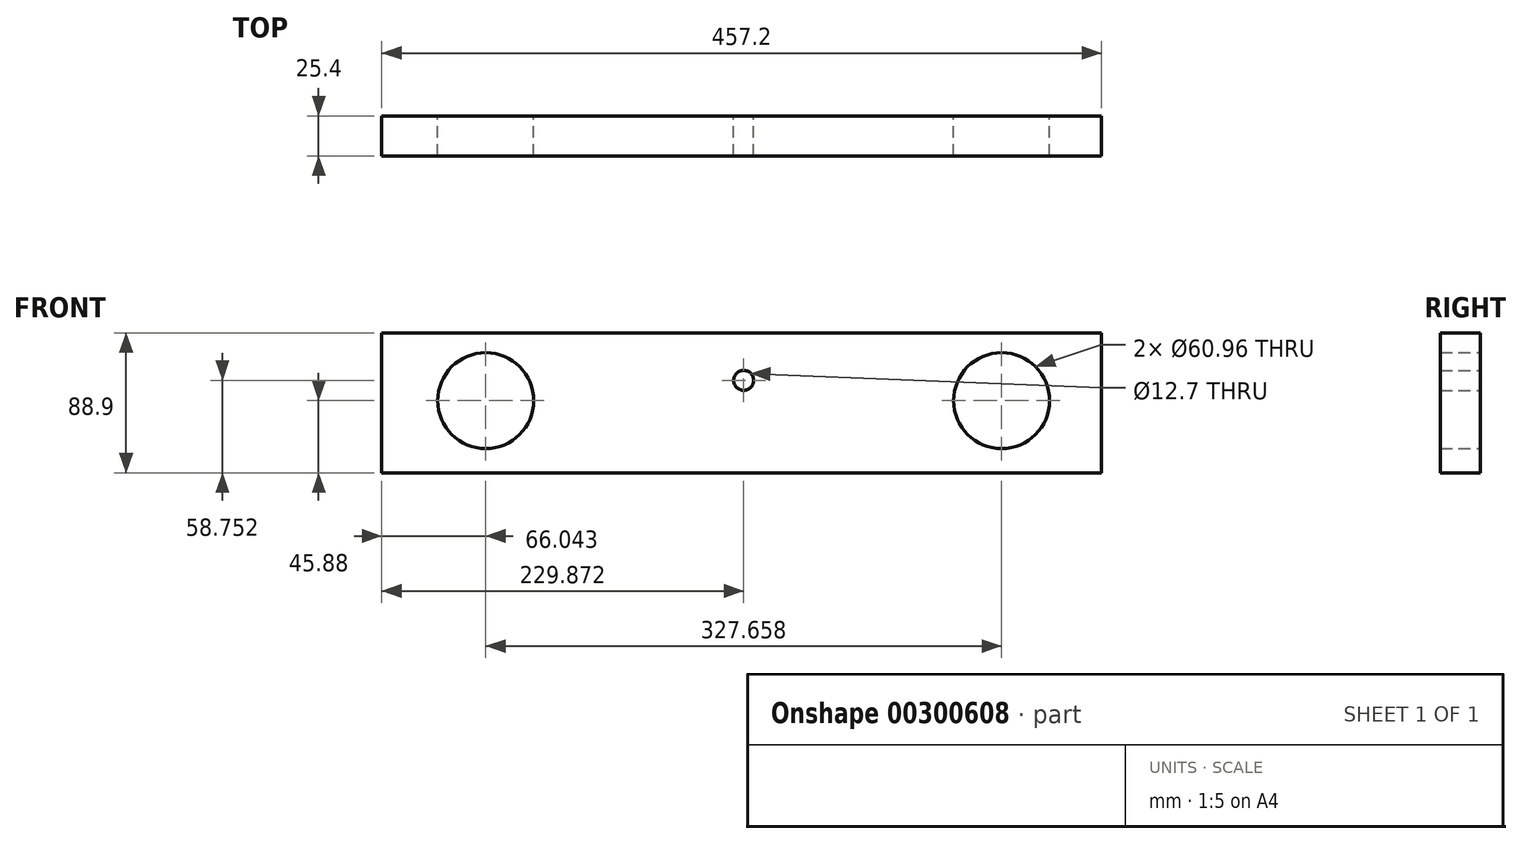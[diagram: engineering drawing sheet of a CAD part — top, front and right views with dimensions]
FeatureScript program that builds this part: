
annotation { "Feature Type Name" : "Feature", "Feature Type Description" : "" }
export const myFeature = defineFeature(function(context is Context, id is Id, definition is map)
    precondition{}
    {
        {
            var Q0;
            Q0=qCreatedBy(makeId("Front.planeOp"),FACE);
            var sketch = newSketch(context, id + "F0", { "sketchPlane" : qUnion([Q0])});
            skLineSegment(sketch, "E0", {"start": v(-310.3, 43.02) * mm, "end": v(-310.3, -45.88) * mm});
            skCircle(sketch, "E1", {"center": v(-244.27, 0) * mm, "radius": 30.48 * mm});
            skCircle(sketch, "E2", {"center": v(83.4, 0) * mm, "radius": 30.48 * mm});
            skPoint(sketch, "E3.endSnap0", {"position": v(273.9, -1.43) * mm});
            skLineSegment(sketch, "E4", {"start": v(-310.3, 43.02) * mm, "end": v(146.9, 43.02) * mm});
            skLineSegment(sketch, "E5", {"start": v(146.9, 43.02) * mm, "end": v(146.9, -45.88) * mm});
            skLineSegment(sketch, "E6", {"start": v(146.9, -45.88) * mm, "end": v(-310.3, -45.88) * mm});
            skLineSegment(sketch, "E7", {"start": v(-244.27, -30.48) * mm, "end": v(83.4, -30.48) * mm, "construction": true});
            skLineSegment(sketch, "E8", {"start": v(83.4, -30.48) * mm, "end": v(83.4, 30.48) * mm, "construction": true});
            skLineSegment(sketch, "E9", {"start": v(83.4, 30.48) * mm, "end": v(-244.27, 30.48) * mm, "construction": true});
            skLineSegment(sketch, "E10", {"start": v(-244.27, 30.48) * mm, "end": v(-244.27, -30.48) * mm, "construction": true});
            skCircle(sketch, "E11", {"center": v(-80.44, 12.87) * mm, "radius": 6.35 * mm});
            skPoint(sketch, "E11.centerSnap0", {"position": v(-80.44, 30.48) * mm});
            skLineSegment(sketch, "E12", {"start": v(-213.79, 0) * mm, "end": v(52.91, 0) * mm, "construction": true});
            skSolve(sketch);
        }
        {
            var Q0;
            Q0=makeQuery(id+"F0.imprint","IMPRINT",FACE,{"disambiguationData":[TD([[makeQuery(id+"F0.imprint","IMPRINT",EDGE,{"derivedFrom":sQuery(id+"F0.wireOp",EDGE,"E0")}),1.0]])]});
            extrude(context, id + "F1", {"entities" : qUnion([Q0]), "depth" : 25.4 * mm});
        }
    });
